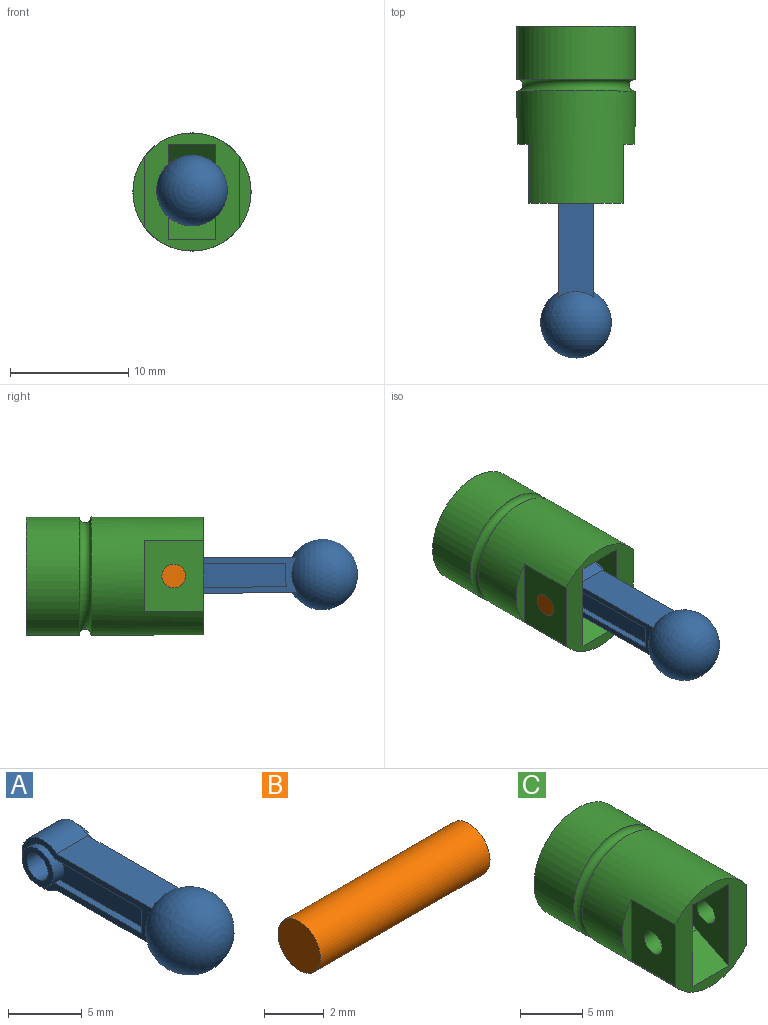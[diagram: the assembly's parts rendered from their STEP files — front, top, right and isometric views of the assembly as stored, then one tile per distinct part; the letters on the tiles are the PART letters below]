
ASSEMBLY  parts=3 mates=2
PART A: 19 faces, bbox 6x17.6x6 mm
  f0: sphere r=3mm, area 103.2mm2, adj f1,f3,f5,f6
  f1: plane 9.15x3mm, normal (0,0,-1), area 26.5mm2, adj f0,f2,f5,f6
  f2: cylinder r=2mm len=4mm, axis (-1,0,0), area 27.5mm2, adj f1,f3,f5,f6
  f3: plane 9.15x3mm, normal (0,0,1), area 26.5mm2, adj f0,f2,f5,f6
  f4: cylinder r=1mm len=4mm, axis (-1,0,0), area 25.1mm2, adj f8,f14
  f5: plane 12.48x4mm, normal (1,0,0), area 14.3mm2, adj f0,f1,f2,f3,f7,f9,f10,f11
  f6: plane 12.48x4mm, normal (-1,0,0), area 14.3mm2, adj f0,f1,f2,f3,f13,f15,f16,f17
  f7: cylinder r=1.5mm len=3mm, axis (-1,0,0), area 5.8mm2, adj f5,f8,f9,f11,f12
  f8: plane 3x3mm, normal (1,0,0), area 3.9mm2, adj f4,f7
  f9: plane 8.38x0.5mm, normal (0,0,-1), area 4.2mm2, adj f5,f7,f10,f12
  f10: plane 2x0.5mm, normal (0,1,0), area 1mm2, adj f5,f9,f11,f12
  f11: plane 8.38x0.5mm, normal (0,0,1), area 4.2mm2, adj f5,f7,f10,f12
  f12: plane 8.38x2mm, normal (1,0,0), area 16.2mm2, adj f7,f9,f10,f11
  f13: cylinder r=1.5mm len=3mm, axis (1,0,0), area 5.8mm2, adj f6,f14,f15,f16,f18
  f14: plane 3x3mm, normal (-1,0,0), area 3.9mm2, adj f4,f13
  f15: plane 8.38x0.5mm, normal (0,0,-1), area 4.2mm2, adj f6,f13,f17,f18
  f16: plane 8.38x0.5mm, normal (0,0,1), area 4.2mm2, adj f6,f13,f17,f18
  f17: plane 2x0.5mm, normal (0,1,0), area 1mm2, adj f6,f15,f16,f18
  f18: plane 8.38x2mm, normal (-1,0,0), area 16.2mm2, adj f13,f15,f16,f17
PART B: 3 faces, bbox 8x2x2 mm
  f0: cylinder r=1mm len=8mm, axis (-1,0,0), area 50.3mm2, adj f1,f2
  f1: plane 2x2mm, normal (1,0,0), area 3.1mm2, adj f0
  f2: plane 2x2mm, normal (-1,0,0), area 3.1mm2, adj f0
PART C: 16 faces, bbox 11.6x15x11.6 mm
  f0: cylinder r=5mm len=10mm, axis (0,-1,0), area 234.1mm2, adj f1,f7,f8,f9,f10,f11
  f1: plane 10x8mm, normal (0,-1,0), area 38.4mm2, adj f0,f2,f4,f5,f6,f7,f9
  f2: plane 4x3.6mm, normal (0,-0.44,0.9), area 16mm2, adj f1,f3,f5,f6
  f3: cylinder r=2.5mm len=4.49mm, axis (1,0,0), area 22.3mm2, adj f2,f4,f5,f6
  f4: plane 4x3.6mm, normal (0,-0.44,-0.9), area 16mm2, adj f1,f3,f5,f6
  f5: plane 8x5mm, normal (1,0,0), area 23.8mm2, adj f1,f2,f3,f4,f14
  f6: plane 8x5mm, normal (-1,0,0), area 23.8mm2, adj f1,f2,f3,f4,f15
  f7: plane 6x5mm, normal (1,0,0), area 26.9mm2, adj f0,f1,f8,f15
  f8: plane 6x1mm, normal (0,-1,0), area 4.1mm2, adj f0,f7
  f9: plane 6x5mm, normal (-1,0,0), area 26.9mm2, adj f0,f1,f10,f14
  f10: plane 6x1mm, normal (0,-1,0), area 4.1mm2, adj f0,f9
  f11: torus R=5mm, axis (0,-1,0), area 46.2mm2, adj f0,f13
  f12: plane 10x10mm, normal (0,1,0), area 78.5mm2, adj f13
  f13: cylinder r=5mm len=10mm, axis (0,-1,0), area 141.4mm2, adj f11,f12
  f14: cylinder r=1mm len=2mm, axis (1,0,0), area 12.6mm2, adj f5,f9
  f15: cylinder r=1mm len=2mm, axis (1,0,0), area 12.6mm2, adj f6,f7
PLACE A rot(axis=(-1,0,0),0.6deg) t=(0.76,-4.09,1.81)mm
PLACE B t=(0.76,-4.09,1.81)mm
PLACE C t=(0.76,-6.59,1.81)mm
MATE revolute B.f0 <-> C.f14  axis (1,0,0) through (4.76,-4.09,1.81)mm
MATE revolute B.f0 <-> A.f4  axis (-1,0,0) through (0.76,-4.09,1.81)mm
